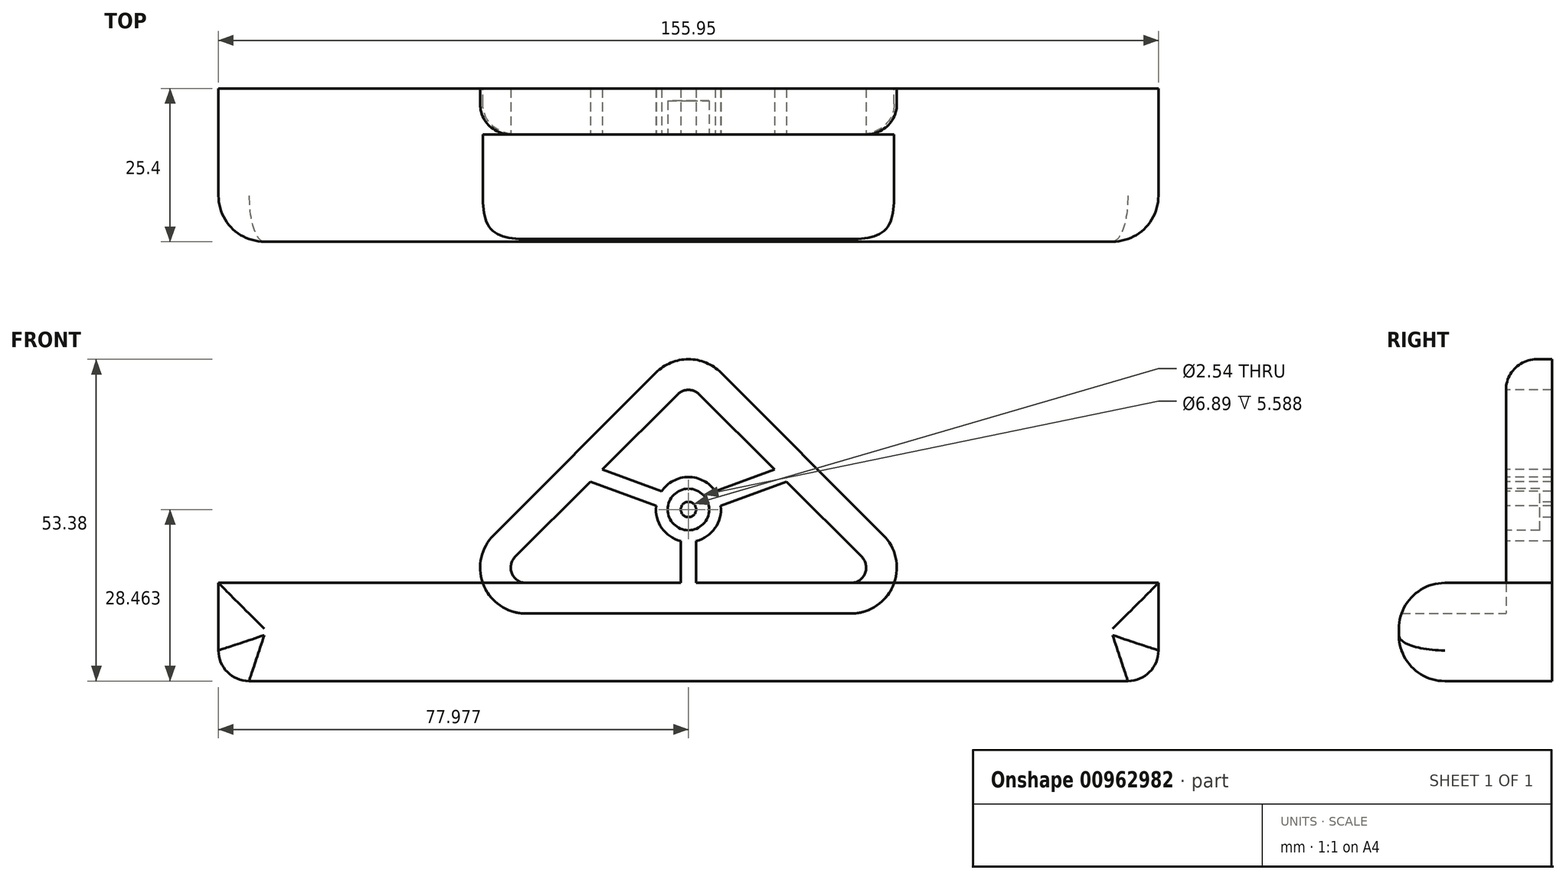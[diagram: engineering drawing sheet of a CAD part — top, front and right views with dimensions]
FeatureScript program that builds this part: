
annotation { "Feature Type Name" : "Feature", "Feature Type Description" : "" }
export const myFeature = defineFeature(function(context is Context, id is Id, definition is map)
    precondition{}
    {
        {
            var Q0;
            Q0=qCreatedBy(makeId("Front.planeOp"),FACE);
            var sketch = newSketch(context, id + "F0", { "sketchPlane" : qUnion([Q0])});
            skLineSegment(sketch, "E0", {"start": v(-6.13, 0) * mm, "end": v(-60.01, 0) * mm});
            skLineSegment(sketch, "E1", {"start": v(-61.8, 4.34) * mm, "end": v(-34.87, 31.28) * mm});
            skLineSegment(sketch, "E2", {"start": v(-31.28, 31.28) * mm, "end": v(-4.34, 4.34) * mm});
            skPoint(sketch, "E3.visualSharp", {"position": v(-33.07, 33.07) * mm});
            skArc(sketch, "E3.filletArc", {"start": v(-31.28, 31.28) * mm, "mid": v(-33.07, 32.02) * mm, "end": v(-34.87, 31.28) * mm});
            skPoint(sketch, "E4.visualSharp", {"position": v(0, 0) * mm});
            skArc(sketch, "E4.filletArc", {"start": v(-6.13, 0) * mm, "mid": v(-3.79, 1.57) * mm, "end": v(-4.34, 4.34) * mm});
            skPoint(sketch, "E5.visualSharp", {"position": v(-66.15, 0) * mm});
            skArc(sketch, "E5.filletArc", {"start": v(-61.8, 4.34) * mm, "mid": v(-62.36, 1.57) * mm, "end": v(-60.01, 0) * mm});
            skArc(sketch, "E6.0", {"start": v(-65.4, 7.93) * mm, "mid": v(-67.05, -0.38) * mm, "end": v(-60.01, -5.08) * mm});
            skArc(sketch, "E6.1", {"start": v(-27.68, 34.87) * mm, "mid": v(-33.07, 37.1) * mm, "end": v(-38.46, 34.87) * mm});
            skLineSegment(sketch, "E6.2", {"start": v(-27.68, 34.87) * mm, "end": v(-0.74, 7.93) * mm});
            skLineSegment(sketch, "E6.3", {"start": v(-65.4, 7.93) * mm, "end": v(-38.46, 34.87) * mm});
            skArc(sketch, "E6.4", {"start": v(-6.13, -5.08) * mm, "mid": v(0.9, -0.38) * mm, "end": v(-0.74, 7.93) * mm});
            skLineSegment(sketch, "E6.5", {"start": v(-6.13, -5.08) * mm, "end": v(-60.01, -5.08) * mm});
            skCircle(sketch, "E7", {"center": v(-33.07, 12.18) * mm, "radius": 5.38 * mm});
            skLineSegment(sketch, "E8.0", {"start": v(-59.73, 6.41) * mm, "end": v(-48.96, 17.19) * mm});
            skLineSegment(sketch, "E9.0.left", {"start": v(-31.8, 6.96) * mm, "end": v(-31.8, 0) * mm});
            skLineSegment(sketch, "E9.0.right", {"start": v(-34.34, 6.96) * mm, "end": v(-34.34, 0) * mm});
            skLineSegment(sketch, "E10.0.left", {"start": v(-28.6, 15.18) * mm, "end": v(-18.8, 18.8) * mm});
            skLineSegment(sketch, "E10.0.right", {"start": v(-27.73, 12.8) * mm, "end": v(-16.82, 16.82) * mm});
            skLineSegment(sketch, "E11.0.left", {"start": v(-38.42, 12.8) * mm, "end": v(-49.33, 16.82) * mm});
            skLineSegment(sketch, "E11.0.right", {"start": v(-37.54, 15.18) * mm, "end": v(-47.35, 18.8) * mm});
            skCircle(sketch, "E12", {"center": v(-33.07, 12.18) * mm, "radius": 3.44 * mm});
            skCircle(sketch, "E13", {"center": v(-33.07, 12.18) * mm, "radius": 1.27 * mm});
            skSolve(sketch);
        }
        {
            var Q0;
            Q0=makeQuery(id+"F0.imprint","IMPRINT",FACE,{"disambiguationData":[TD([[makeQuery(id+"F0.imprint","IMPRINT",EDGE,{"derivedFrom":sQuery(id+"F0.wireOp",EDGE,"E0")}),1.0]])]});
            var Q1;
            {var subQ0=sQuery(id+"F0.wireOp",EDGE,"E11.0.left");Q1=makeQuery(id+"F0.imprint","IMPRINT",FACE,{"disambiguationData":[TD([[makeQuery(id+"F0.imprint","IMPRINT",EDGE,{"derivedFrom":subQ0}),-1.0]])]});}
            var Q2;
            {var subQ0=sQuery(id+"F0.wireOp",EDGE,"E7");var subQ4=makeQuery(id+"F0.imprint","INTERSECT",VERTEX,{"derivedFrom":[subQ0,sQuery(id+"F0.wireOp",EDGE,"E10.0.left")]});Q2=makeQuery(id+"F0.imprint","IMPRINT",FACE,{"disambiguationData":[TD([[makeQuery(id+"F0.imprint","IMPRINT",EDGE,{"disambiguationData":[TD([[subQ4,1.0]])],"derivedFrom":subQ0}),1.0]])]});}
            var Q3;
            {var subQ0=sQuery(id+"F0.wireOp",EDGE,"E10.0.left");Q3=makeQuery(id+"F0.imprint","IMPRINT",FACE,{"disambiguationData":[TD([[makeQuery(id+"F0.imprint","IMPRINT",EDGE,{"derivedFrom":subQ0}),-1.0]])]});}
            var Q4;
            {var subQ0=sQuery(id+"F0.wireOp",EDGE,"E9.0.left");Q4=makeQuery(id+"F0.imprint","IMPRINT",FACE,{"disambiguationData":[TD([[makeQuery(id+"F0.imprint","IMPRINT",EDGE,{"derivedFrom":subQ0}),-1.0]])]});}
            var Q5;
            Q5=makeQuery(id+"F0.imprint","IMPRINT",FACE,{"disambiguationData":[TD([[makeQuery(id+"F0.imprint","IMPRINT",EDGE,{"derivedFrom":sQuery(id+"F0.wireOp",EDGE,"E12")}),1.0]])]});
            extrude(context, id + "F1", {"entities" : qUnion([Q0, Q1, Q2, Q3, Q4, Q5]), "surfaceOperationType" : NewSurfaceOperationType.ADD, "oppositeDirection" : true, "depth" : 7.62 * mm, "offsetDistance" : 25.4 * mm});
        }
        {
            var Q0;
            Q0=makeQuery(id+"F1.opExtrude","CAP_FACE",FACE,{"disambiguationData":[OSD([sQuery(id+"F0.wireOp",EDGE,"E0"),sQuery(id+"F0.wireOp",EDGE,"E1"),sQuery(id+"F0.wireOp",EDGE,"E2"),sQuery(id+"F0.wireOp",EDGE,"E3.filletArc"),sQuery(id+"F0.wireOp",EDGE,"E4.filletArc"),sQuery(id+"F0.wireOp",EDGE,"E5.filletArc"),sQuery(id+"F0.wireOp",EDGE,"E6.0"),sQuery(id+"F0.wireOp",EDGE,"E6.1"),sQuery(id+"F0.wireOp",EDGE,"E6.2"),sQuery(id+"F0.wireOp",EDGE,"E6.3"),sQuery(id+"F0.wireOp",EDGE,"E6.4"),sQuery(id+"F0.wireOp",EDGE,"E6.5"),sQuery(id+"F0.wireOp",EDGE,"E7"),sQuery(id+"F0.wireOp",EDGE,"E8.0"),sQuery(id+"F0.wireOp",EDGE,"E9.0.left"),sQuery(id+"F0.wireOp",EDGE,"E9.0.right"),sQuery(id+"F0.wireOp",EDGE,"E10.0.left"),sQuery(id+"F0.wireOp",EDGE,"E10.0.right"),sQuery(id+"F0.wireOp",EDGE,"E11.0.left"),sQuery(id+"F0.wireOp",EDGE,"E11.0.right")])],"isStart":false});
            var sketch = newSketch(context, id + "F2", { "sketchPlane" : qUnion([Q0])});
            skLineSegment(sketch, "E14", {"start": v(31.8, 0) * mm, "end": v(111.05, 0) * mm});
            skLineSegment(sketch, "E15", {"start": v(111.05, 0) * mm, "end": v(111.05, -16.28) * mm});
            skLineSegment(sketch, "E16", {"start": v(111.05, -16.28) * mm, "end": v(-44.9, -16.28) * mm});
            skLineSegment(sketch, "E17", {"start": v(-44.9, -16.28) * mm, "end": v(-44.9, 0) * mm});
            skLineSegment(sketch, "E18", {"start": v(-44.9, 0) * mm, "end": v(34.34, 0) * mm});
            skLineSegment(sketch, "E19", {"start": v(34.34, 0) * mm, "end": v(31.8, 0) * mm});
            skSolve(sketch);
        }
        {
            var Q0;
            {var subQ1=sQuery(id+"F2.wireOp",EDGE,"E15");Q0=makeQuery(id+"F2.imprint","IMPRINT",FACE,{"disambiguationData":[TD([[makeQuery(id+"F2.imprint","IMPRINT",EDGE,{"derivedFrom":subQ1}),-1.0]])]});}
            extrude(context, id + "F3", {"entities" : qUnion([Q0]), "operationType" : NewBodyOperationType.ADD, "oppositeDirection" : true, "depth" : 25.4 * mm, "offsetDistance" : 25.4 * mm});
        }
        {
            var Q0;
            Q0=makeQuery(id+"F0.imprint","IMPRINT",FACE,{"disambiguationData":[TD([[makeQuery(id+"F0.imprint","IMPRINT",EDGE,{"derivedFrom":sQuery(id+"F0.wireOp",EDGE,"E12")}),1.0]])]});
            extrude(context, id + "F4", {"entities" : qUnion([Q0]), "operationType" : NewBodyOperationType.REMOVE, "oppositeDirection" : true, "depth" : 5.6 * mm, "offsetDistance" : 25.4 * mm});
        }
        {
            var Q0;
            {var subQ0=sQuery(id+"F0.wireOp",EDGE,"E6.4");Q0=makeQuery(id+"F3.boolean.opBoolean","SPLIT",EDGE,{"disambiguationData":[topologyDisambiguationEdgeConnected([makeQuery(id+"F3.opExtrude","SWEPT_FACE",FACE,{"disambiguationData":[OSD([subQ0])]})])],"derivedFrom":makeQuery(id+"F1.opExtrude","CAP_EDGE",EDGE,{"disambiguationData":[OSD([subQ0])],"isStart":true})});}
            fillet(context, id + "F5", {"entities" : qUnion([Q0]), "radius" : 5.08 * mm, "tangentPropagation" : true, "allowEdgeOverflow" : false});
        }
        {
            var Q0;
            Q0=makeQuery(id+"F3.opExtrude","CAP_EDGE",EDGE,{"disambiguationData":[OSD([sQuery(id+"F2.wireOp",EDGE,"E18")])],"isStart":false});
            var Q1;
            Q1=makeQuery(id+"F3.opExtrude","CAP_EDGE",EDGE,{"disambiguationData":[OSD([sQuery(id+"F2.wireOp",EDGE,"E14")])],"isStart":false});
            var Q2;
            Q2=makeQuery(id+"F3.opExtrude","CAP_EDGE",EDGE,{"disambiguationData":[OSD([sQuery(id+"F2.wireOp",EDGE,"E15")])],"isStart":false});
            var Q3;
            Q3=makeQuery(id+"F3.opExtrude","CAP_EDGE",EDGE,{"disambiguationData":[OSD([sQuery(id+"F2.wireOp",EDGE,"E16")])],"isStart":false});
            var Q4;
            Q4=makeQuery(id+"F3.opExtrude","CAP_EDGE",EDGE,{"disambiguationData":[OSD([sQuery(id+"F2.wireOp",EDGE,"E17")])],"isStart":false});
            fillet(context, id + "F6", {"entities" : qUnion([Q0, Q1, Q2, Q3, Q4]), "radius" : 7.62 * mm, "tangentPropagation" : true, "allowEdgeOverflow" : false});
        }
        {
            var Q0;
            Q0=makeQuery(id+"F6.opFillet","BLEND_EDGE",EDGE,{"blendedFrom":[makeQuery(id+"F3.opExtrude","CAP_EDGE",EDGE,{"disambiguationData":[OSD([sQuery(id+"F2.wireOp",EDGE,"E15")])],"isStart":false}),makeQuery(id+"F3.opExtrude","CAP_EDGE",EDGE,{"disambiguationData":[OSD([sQuery(id+"F2.wireOp",EDGE,"E18")])],"isStart":false})],"blendedInto":[]});
            var Q1;
            Q1=makeQuery(id+"F6.opFillet","BLEND_EDGE",EDGE,{"blendedFrom":[makeQuery(id+"F3.opExtrude","CAP_EDGE",EDGE,{"disambiguationData":[OSD([sQuery(id+"F2.wireOp",EDGE,"E15")])],"isStart":false}),makeQuery(id+"F3.opExtrude","CAP_EDGE",EDGE,{"disambiguationData":[OSD([sQuery(id+"F2.wireOp",EDGE,"E16")])],"isStart":false})],"blendedInto":[]});
            var Q2;
            Q2=makeQuery(id+"F6.opFillet","BLEND_EDGE",EDGE,{"blendedFrom":[makeQuery(id+"F3.opExtrude","CAP_EDGE",EDGE,{"disambiguationData":[OSD([sQuery(id+"F2.wireOp",EDGE,"E17")])],"isStart":false}),makeQuery(id+"F3.opExtrude","CAP_EDGE",EDGE,{"disambiguationData":[OSD([sQuery(id+"F2.wireOp",EDGE,"E18")])],"isStart":false})],"blendedInto":[]});
            var Q3;
            Q3=makeQuery(id+"F6.opFillet","BLEND_EDGE",EDGE,{"blendedFrom":[makeQuery(id+"F3.opExtrude","CAP_EDGE",EDGE,{"disambiguationData":[OSD([sQuery(id+"F2.wireOp",EDGE,"E16")])],"isStart":false}),makeQuery(id+"F3.opExtrude","CAP_EDGE",EDGE,{"disambiguationData":[OSD([sQuery(id+"F2.wireOp",EDGE,"E17")])],"isStart":false})],"blendedInto":[]});
            fillet(context, id + "F7", {"entities" : qUnion([Q0, Q1, Q2, Q3]), "radius" : 5.08 * mm, "tangentPropagation" : true, "allowEdgeOverflow" : false});
        }
    });
